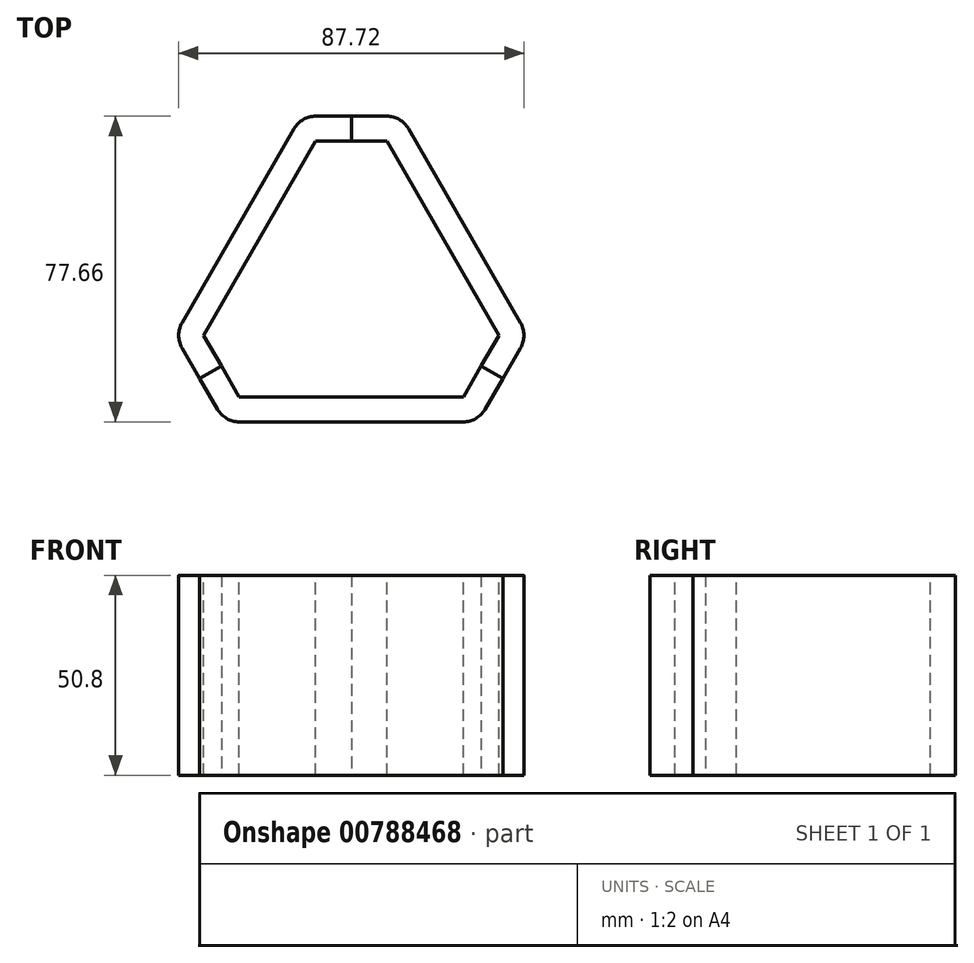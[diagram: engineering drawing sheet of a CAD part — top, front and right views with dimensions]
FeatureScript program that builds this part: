
annotation { "Feature Type Name" : "Feature", "Feature Type Description" : "" }
export const myFeature = defineFeature(function(context is Context, id is Id, definition is map)
    precondition{}
    {
        {
            var Q0;
            Q0=qCreatedBy(makeId("Top.planeOp"),FACE);
            var sketch = newSketch(context, id + "F0", { "sketchPlane" : qUnion([Q0])});
            skLineSegment(sketch, "E0", {"start": v(0, 0) * mm, "end": v(0, 44.44) * mm});
            skLineSegment(sketch, "E1", {"start": v(0, 44.44) * mm, "end": v(12.7, 44.44) * mm});
            skLineSegment(sketch, "E2", {"start": v(12.7, 44.44) * mm, "end": v(28.77, 16.61) * mm});
            skLineSegment(sketch, "E3", {"start": v(28.77, 16.61) * mm, "end": v(0, 0) * mm});
            skSolve(sketch);
        }
        {
            var Q0;
            Q0=makeQuery(id+"F0.imprint","IMPRINT",FACE,{"disambiguationData":[TD([[makeQuery(id+"F0.imprint","IMPRINT",EDGE,{"derivedFrom":sQuery(id+"F0.wireOp",EDGE,"E0")}),-1.0]])]});
            extrude(context, id + "F1", {"entities" : qUnion([Q0]), "depth" : 50.8 * mm, "offsetDistance" : 25.4 * mm});
        }
        {
            var Q0;
            Q0=makeQuery(id+"F1.opExtrude","SWEPT_EDGE",EDGE,{"disambiguationData":[OSD([sQuery(id+"F0.wireOp",EDGE,"E1"),sQuery(id+"F0.wireOp",EDGE,"E2")])]});
            fillet(context, id + "F2", {"entities" : qUnion([Q0]), "radius" : 6.35 * mm, "tangentPropagation" : true, "allowEdgeOverflow" : false});
        }
        {
            var Q0;
            Q0=makeQuery(id+"F1.opExtrude","SWEPT_FACE",FACE,{"disambiguationData":[OSD([sQuery(id+"F0.wireOp",EDGE,"E0")])]});
            var Q1;
            Q1=makeQuery(id+"F1.opExtrude","CAP_FACE",FACE,{"disambiguationData":[OSD([sQuery(id+"F0.wireOp",EDGE,"E0"),sQuery(id+"F0.wireOp",EDGE,"E1"),sQuery(id+"F0.wireOp",EDGE,"E2"),sQuery(id+"F0.wireOp",EDGE,"E3")])],"isStart":false});
            var Q2;
            Q2=makeQuery(id+"F1.opExtrude","SWEPT_FACE",FACE,{"disambiguationData":[OSD([sQuery(id+"F0.wireOp",EDGE,"E3")])]});
            var Q3;
            Q3=makeQuery(id+"F1.opExtrude","CAP_FACE",FACE,{"disambiguationData":[OSD([sQuery(id+"F0.wireOp",EDGE,"E0"),sQuery(id+"F0.wireOp",EDGE,"E1"),sQuery(id+"F0.wireOp",EDGE,"E2"),sQuery(id+"F0.wireOp",EDGE,"E3")])],"isStart":true});
            shell(context, id + "F3", {"entities" : qUnion([Q0, Q1, Q2, Q3]), "thickness" : 6.35 * mm});
        }
        {
            var Q0;
            Q0=makeQuery(id+"F1.opExtrude","SWEPT_BODY",BODY,{"disambiguationData":[OSD([sQuery(id+"F0.wireOp",EDGE,"E0"),sQuery(id+"F0.wireOp",EDGE,"E1"),sQuery(id+"F0.wireOp",EDGE,"E2"),sQuery(id+"F0.wireOp",EDGE,"E3")])]});
            var Q1;
            Q1=makeQuery(id+"F1.opExtrude","SWEPT_FACE",FACE,{"disambiguationData":[OSD([sQuery(id+"F0.wireOp",EDGE,"E3")])]});
            mirror(context, id + "F4", {"operationType" : NewBodyOperationType.ADD, "entities" : qUnion([Q0]), "mirrorPlane" : qUnion([Q1])});
        }
        {
            var Q0;
            Q0=qCreatedBy(makeId("Right.planeOp"),FACE);
            var sketch = newSketch(context, id + "F5", { "sketchPlane" : qUnion([Q0])});
            skLineSegment(sketch, "E4", {"start": v(0, 75.98) * mm, "end": v(0, 0) * mm});
            skSolve(sketch);
        }
        {
            var Q0;
            Q0=makeQuery(id+"F1.opExtrude","SWEPT_BODY",BODY,{"disambiguationData":[OSD([sQuery(id+"F0.wireOp",EDGE,"E0"),sQuery(id+"F0.wireOp",EDGE,"E1"),sQuery(id+"F0.wireOp",EDGE,"E2"),sQuery(id+"F0.wireOp",EDGE,"E3")])]});
            var Q1;
            Q1=sQuery(id+"F5.wireOp",EDGE,"E4");
            circularPattern(context, id + "F6", {"entities" : qUnion([Q0]), "axis" : qUnion([Q1]), "angle" : 360 * degree, "instanceCount" : 3, "equalSpace" : true});
        }
    });
